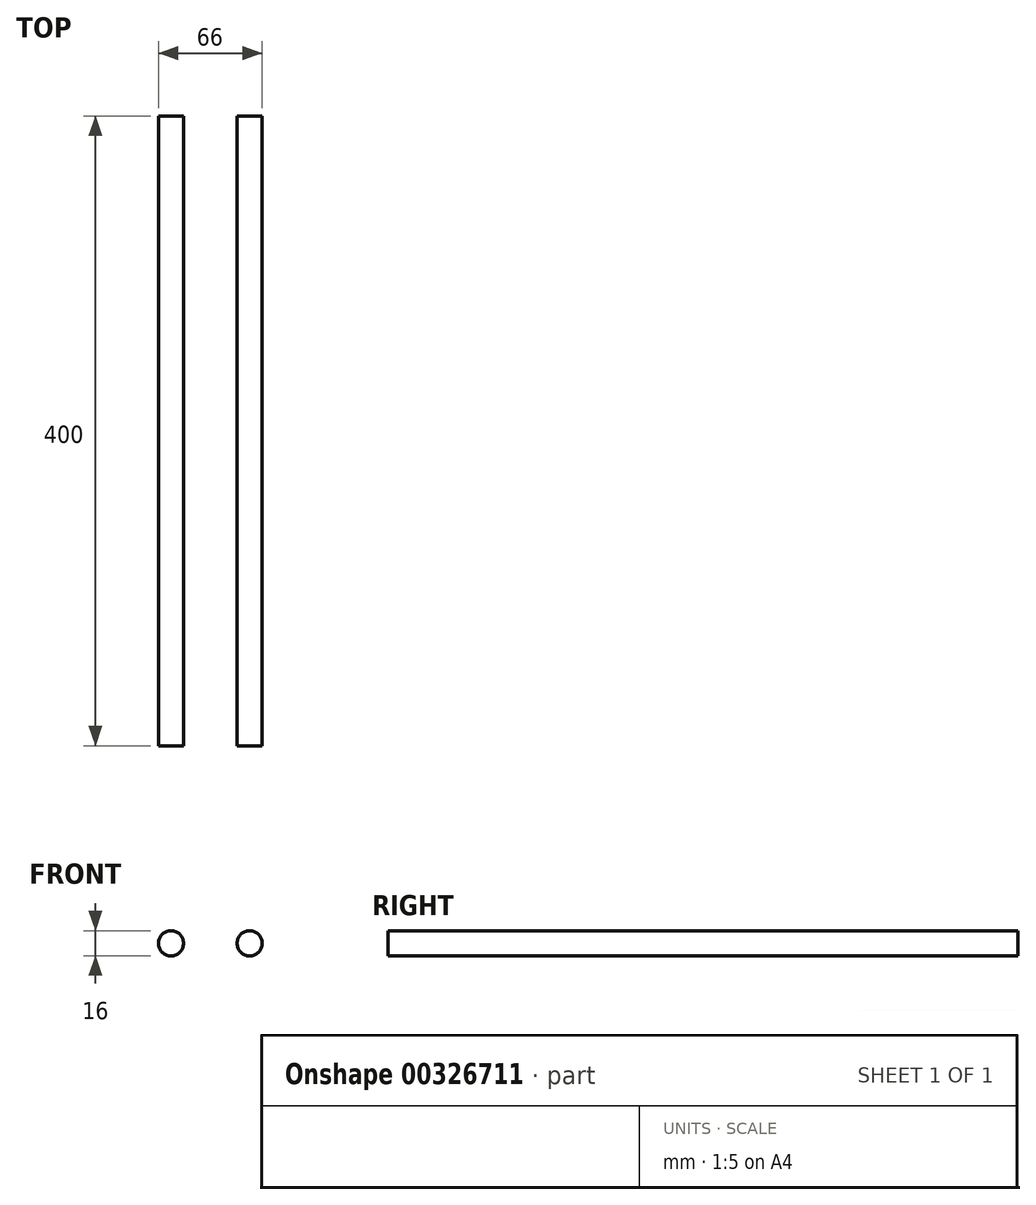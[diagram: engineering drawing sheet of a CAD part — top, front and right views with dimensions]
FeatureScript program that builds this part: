
annotation { "Feature Type Name" : "Feature", "Feature Type Description" : "" }
export const myFeature = defineFeature(function(context is Context, id is Id, definition is map)
    precondition{}
    {
        {
            assignVariable(context, id + "F0", {"name" : "LARGO_VARI", "anyValue" : 400});
        }
        {
            var Q0;
            Q0=qCreatedBy(makeId("Front.planeOp"),FACE);
            var sketch = newSketch(context, id + "F1", { "sketchPlane" : qUnion([Q0])});
            skCircle(sketch, "E0", {"center": v(30, 8) * mm, "radius": 8 * mm});
            skPoint(sketch, "E1", {"position": v(30, 0) * mm});
            skCircle(sketch, "E2", {"center": v(80, 8) * mm, "radius": 8 * mm});
            skPoint(sketch, "E3", {"position": v(80, 0) * mm});
            skSolve(sketch);
        }
        {
            var Q0;
            Q0=makeQuery(id+"F1.imprint","IMPRINT",FACE,{"disambiguationData":[TD([[makeQuery(id+"F1.imprint","IMPRINT",EDGE,{"derivedFrom":sQuery(id+"F1.wireOp",EDGE,"E0")}),1.0]])]});
            var Q1;
            Q1=makeQuery(id+"F1.imprint","IMPRINT",FACE,{"disambiguationData":[TD([[makeQuery(id+"F1.imprint","IMPRINT",EDGE,{"derivedFrom":sQuery(id+"F1.wireOp",EDGE,"E2")}),1.0]])]});
            extrude(context, id + "F2", {"entities" : qUnion([Q0, Q1]), "oppositeDirection" : true, "depth" : (getVariable(context, 'LARGO_VARI')) * mm});
        }
    });
